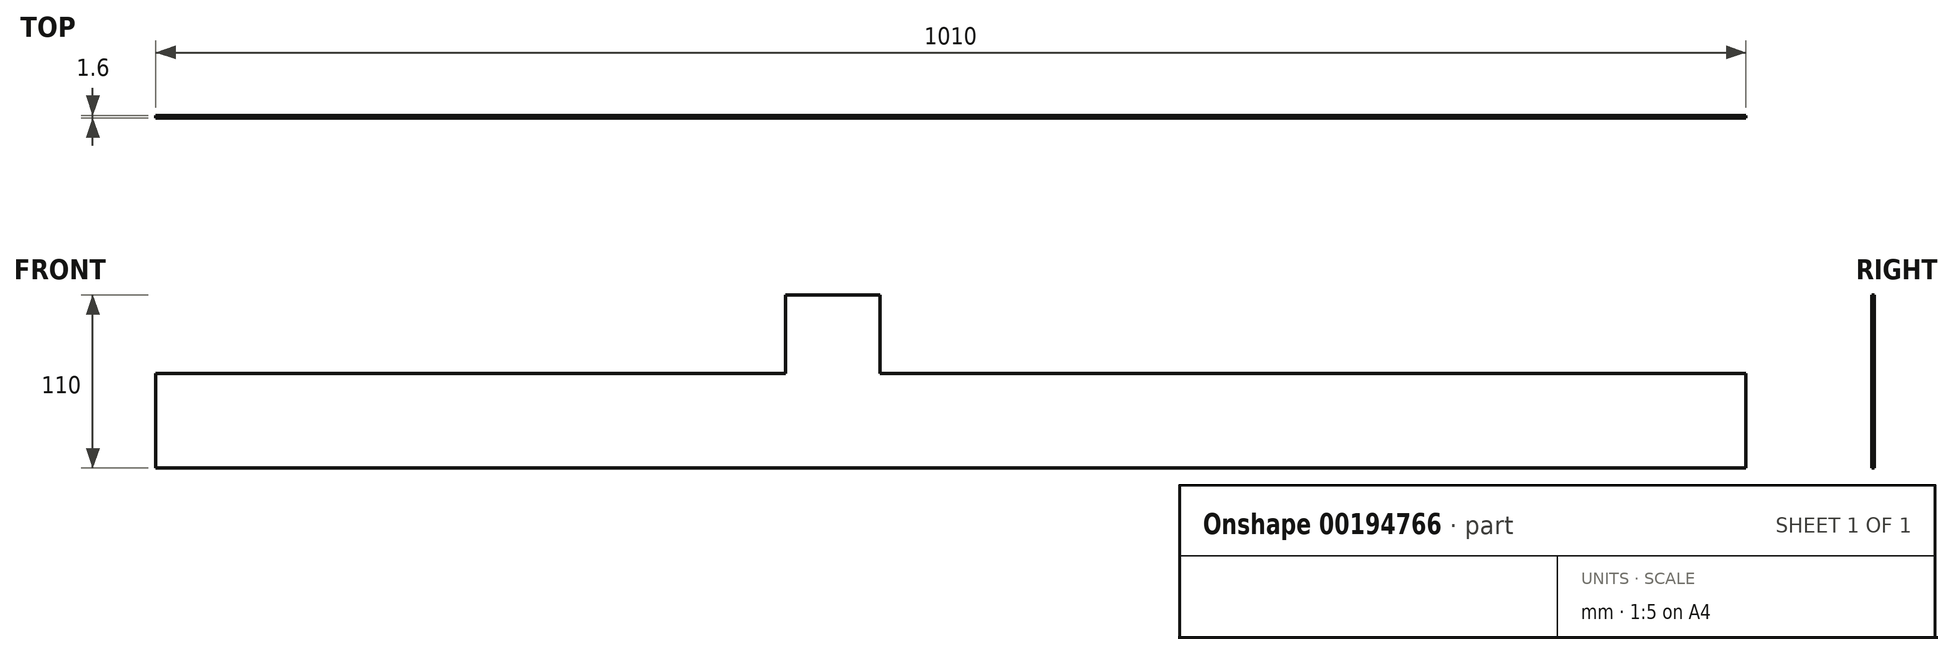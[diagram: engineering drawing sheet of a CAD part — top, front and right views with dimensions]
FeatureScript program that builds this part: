
annotation { "Feature Type Name" : "Feature", "Feature Type Description" : "" }
export const myFeature = defineFeature(function(context is Context, id is Id, definition is map)
    precondition{}
    {
        {
            var Q0;
            Q0=qCreatedBy(makeId("Front.planeOp"),FACE);
            var sketch = newSketch(context, id + "F0", { "sketchPlane" : qUnion([Q0])});
            skLineSegment(sketch, "E0", {"start": v(0, 0) * mm, "end": v(0, 60) * mm});
            skLineSegment(sketch, "E1", {"start": v(0, 60) * mm, "end": v(400, 60) * mm});
            skLineSegment(sketch, "E2", {"start": v(400, 60) * mm, "end": v(400, 110) * mm});
            skLineSegment(sketch, "E3", {"start": v(400, 110) * mm, "end": v(460, 110) * mm});
            skLineSegment(sketch, "E4", {"start": v(460, 110) * mm, "end": v(460, 60) * mm});
            skLineSegment(sketch, "E5", {"start": v(460, 60) * mm, "end": v(1010, 60) * mm});
            skLineSegment(sketch, "E6", {"start": v(1010, 60) * mm, "end": v(1010, 0) * mm});
            skLineSegment(sketch, "E7", {"start": v(1010, 0) * mm, "end": v(0, 0) * mm});
            skSolve(sketch);
        }
        {
            var Q0;
            Q0 = qSketchRegion(id + "F0", true);
            extrude(context, id + "F1", {"entities" : qUnion([Q0]), "depth" : 1.6 * mm});
        }
    });
